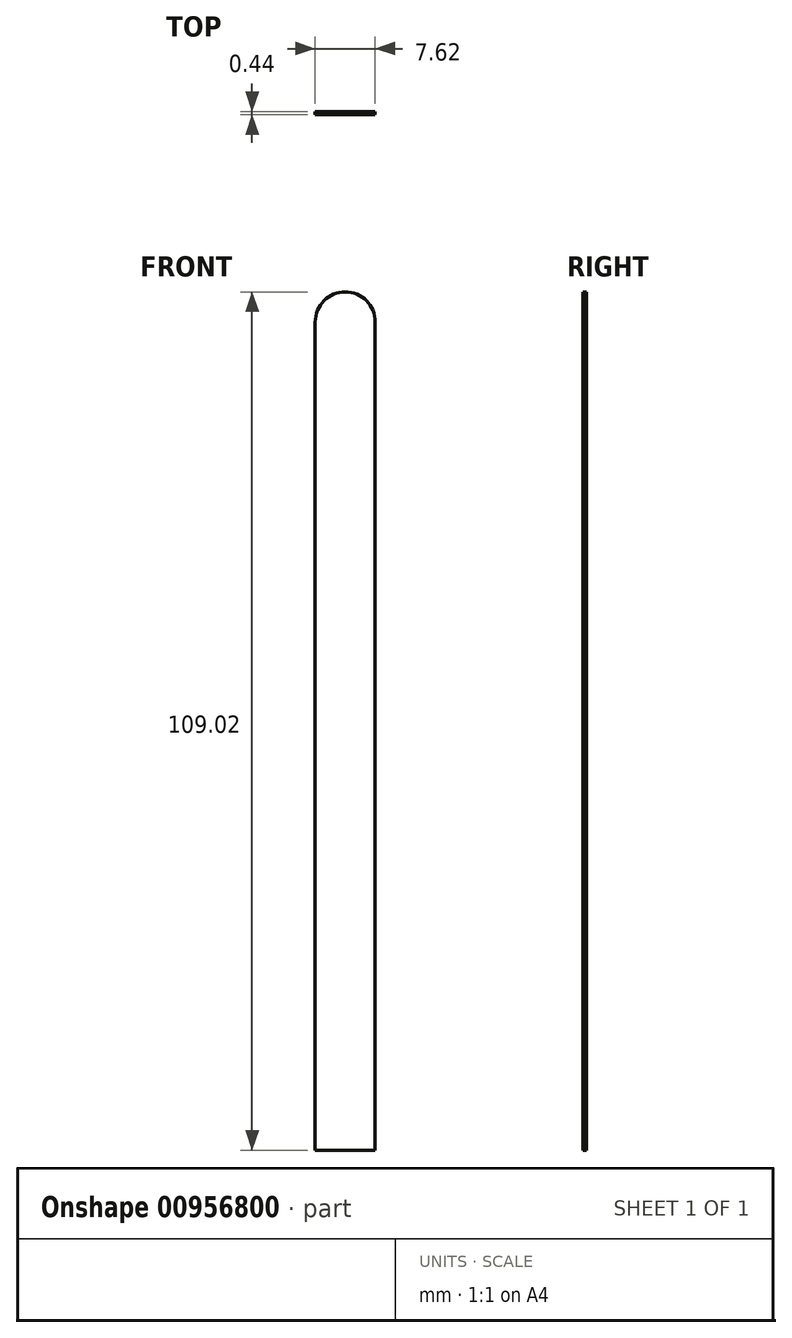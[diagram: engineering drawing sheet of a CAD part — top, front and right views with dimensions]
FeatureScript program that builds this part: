
annotation { "Feature Type Name" : "Feature", "Feature Type Description" : "" }
export const myFeature = defineFeature(function(context is Context, id is Id, definition is map)
    precondition{}
    {
        {
            var Q0;
            Q0=qCreatedBy(makeId("Front.planeOp"),FACE);
            var sketch = newSketch(context, id + "F0", { "sketchPlane" : qUnion([Q0])});
            skLineSegment(sketch, "E0.bottom", {"start": v(-14.37, 48.88) * mm, "end": v(-6.75, 48.88) * mm});
            skLineSegment(sketch, "E0.top", {"start": v(-14.37, -56.33) * mm, "end": v(-6.75, -56.33) * mm});
            skLineSegment(sketch, "E0.left", {"start": v(-14.37, 48.88) * mm, "end": v(-14.37, -56.33) * mm});
            skLineSegment(sketch, "E0.right", {"start": v(-6.75, 48.88) * mm, "end": v(-6.75, -56.33) * mm});
            skArc(sketch, "E1", {"start": v(-6.75, 48.88) * mm, "mid": v(-10.56, 52.7) * mm, "end": v(-14.37, 48.88) * mm});
            skSolve(sketch);
        }
        {
            var Q0;
            Q0=makeQuery(id+"F0.imprint","IMPRINT",FACE,{"disambiguationData":[TD([[makeQuery(id+"F0.imprint","IMPRINT",EDGE,{"derivedFrom":sQuery(id+"F0.wireOp",EDGE,"E0.bottom")}),1.0]])]});
            var Q1;
            Q1=makeQuery(id+"F0.imprint","IMPRINT",FACE,{"disambiguationData":[TD([[makeQuery(id+"F0.imprint","IMPRINT",EDGE,{"derivedFrom":sQuery(id+"F0.wireOp",EDGE,"E0.bottom")}),-1.0]])]});
            extrude(context, id + "F1", {"entities" : qUnion([Q0, Q1]), "depth" : .44 * mm, "offsetDistance" : 25 * mm});
        }
    });
